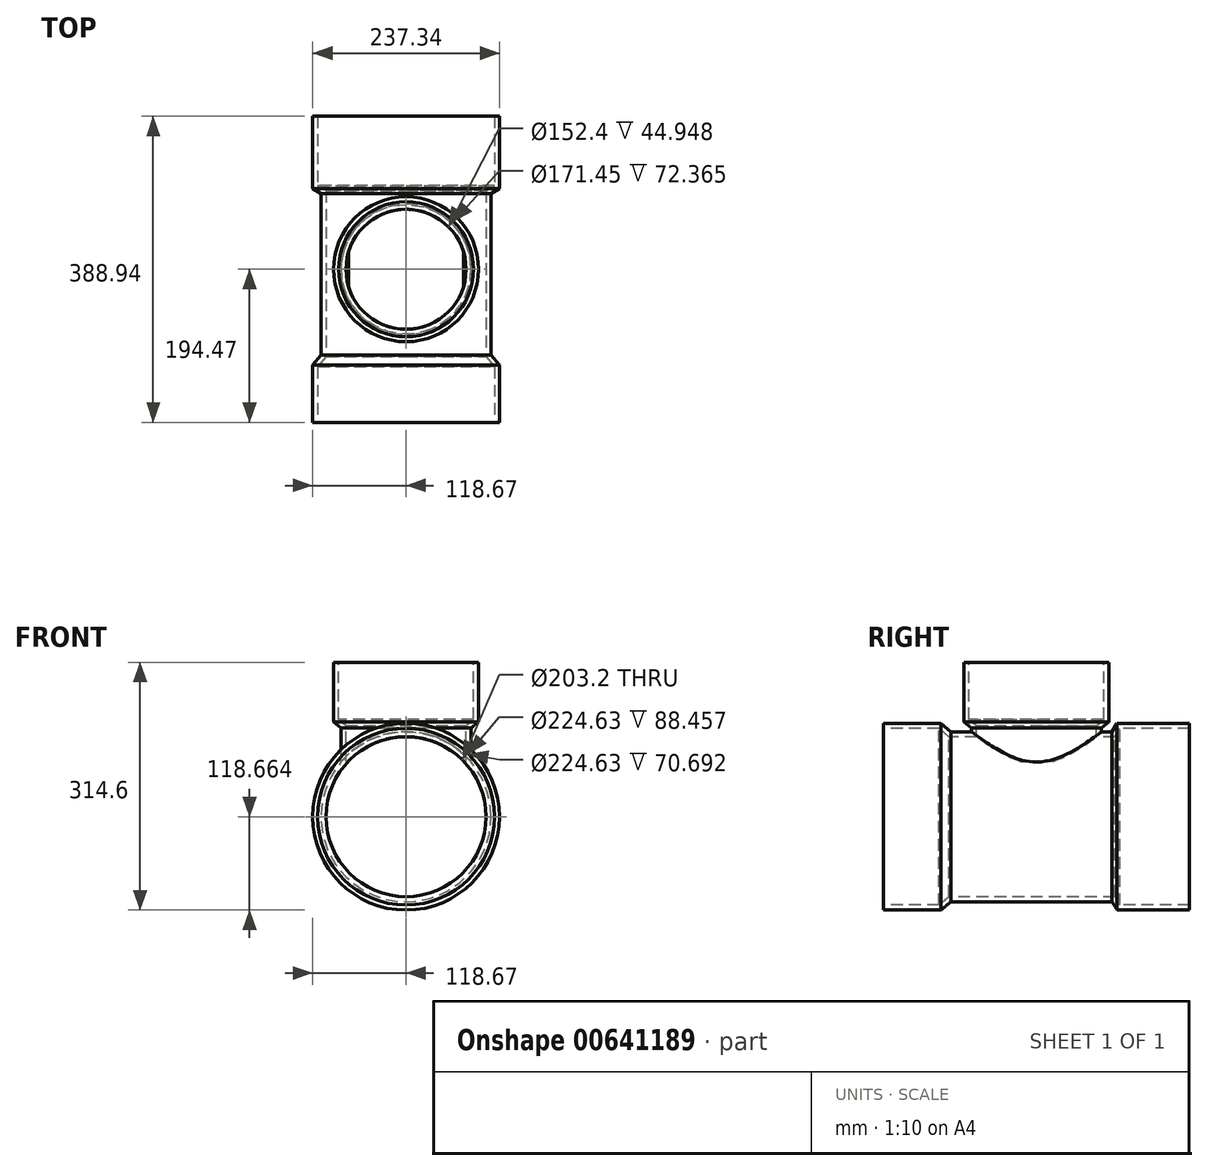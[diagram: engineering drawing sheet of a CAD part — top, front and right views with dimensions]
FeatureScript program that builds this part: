
annotation { "Feature Type Name" : "Feature", "Feature Type Description" : "" }
export const myFeature = defineFeature(function(context is Context, id is Id, definition is map)
    precondition{}
    {
        {
            var Q0;
            Q0=qCreatedBy(makeId("Right.planeOp"),FACE);
            var sketch = newSketch(context, id + "F0", { "sketchPlane" : qUnion([Q0])});
            skLineSegment(sketch, "E0", {"start": v(0, 0) * mm, "end": v(0, -195.94) * mm});
            skLineSegment(sketch, "E1", {"start": v(0, -195.94) * mm, "end": v(194.47, -195.94) * mm, "construction": true});
            skLineSegment(sketch, "E2", {"start": v(194.47, -77.27) * mm, "end": v(102.4, -77.27) * mm});
            skLineSegment(sketch, "E3", {"start": v(96.04, -94.34) * mm, "end": v(96.04, -195.94) * mm, "construction": true});
            skLineSegment(sketch, "E4", {"start": v(0, -195.94) * mm, "end": v(-194.47, -195.94) * mm, "construction": true});
            skLineSegment(sketch, "E5", {"start": v(102.4, -77.27) * mm, "end": v(96.04, -87.99) * mm});
            skLineSegment(sketch, "E6.0", {"start": v(106.01, -83.62) * mm, "end": v(103.42, -87.99) * mm});
            skLineSegment(sketch, "E6.1", {"start": v(194.47, -83.62) * mm, "end": v(106.01, -83.62) * mm});
            skLineSegment(sketch, "E7", {"start": v(96.04, -87.99) * mm, "end": v(-108.74, -87.99) * mm});
            skLineSegment(sketch, "E8.0", {"start": v(96.04, -94.34) * mm, "end": v(-108.74, -94.34) * mm});
            skLineSegment(sketch, "E9", {"start": v(103.42, -87.99) * mm, "end": v(99.66, -94.34) * mm});
            skLineSegment(sketch, "E10", {"start": v(99.66, -94.34) * mm, "end": v(96.04, -94.34) * mm});
            skLineSegment(sketch, "E11", {"start": v(194.47, -77.27) * mm, "end": v(194.47, -83.62) * mm});
            skLineSegment(sketch, "E12", {"start": v(194.47, -83.62) * mm, "end": v(194.47, -195.94) * mm, "construction": true});
            skLineSegment(sketch, "E13", {"start": v(-194.47, -77.27) * mm, "end": v(-121.46, -77.27) * mm});
            skLineSegment(sketch, "E14", {"start": v(-108.74, -94.34) * mm, "end": v(-108.74, -195.94) * mm, "construction": true});
            skLineSegment(sketch, "E15", {"start": v(-121.46, -77.27) * mm, "end": v(-108.74, -87.99) * mm});
            skLineSegment(sketch, "E16.0", {"start": v(-123.78, -83.62) * mm, "end": v(-112.84, -92.84) * mm});
            skLineSegment(sketch, "E16.1", {"start": v(-194.47, -83.62) * mm, "end": v(-123.78, -83.62) * mm});
            skLineSegment(sketch, "E17", {"start": v(-112.84, -92.84) * mm, "end": v(-111.06, -94.34) * mm});
            skLineSegment(sketch, "E18", {"start": v(-111.06, -94.34) * mm, "end": v(-108.74, -94.34) * mm});
            skLineSegment(sketch, "E19", {"start": v(-194.47, -77.27) * mm, "end": v(-194.47, -83.62) * mm});
            skSolve(sketch);
        }
        {
            var Q0;
            Q0=qCreatedBy(makeId("Top.planeOp"),FACE);
            var sketch = newSketch(context, id + "F1", { "sketchPlane" : qUnion([Q0])});
            skCircle(sketch, "E20", {"center": v(0, 0) * mm, "radius": 76.2 * mm});
            skCircle(sketch, "E21.0", {"center": v(0, 0) * mm, "radius": 69.85 * mm});
            skSolve(sketch);
        }
        {
            var Q0;
            Q0=makeQuery(id+"F0.imprint","IMPRINT",FACE,{"disambiguationData":[TD([[makeQuery(id+"F0.imprint","IMPRINT",EDGE,{"derivedFrom":sQuery(id+"F0.wireOp",EDGE,"E2")}),1.0]])]});
            var Q1;
            Q1=makeQuery(id+"F0.imprint","IMPRINT",FACE,{"disambiguationData":[TD([[makeQuery(id+"F0.imprint","IMPRINT",EDGE,{"derivedFrom":sQuery(id+"F0.wireOp",EDGE,"E13")}),-1.0]])]});
            var Q2;
            Q2=sQuery(id+"F0.wireOp",EDGE,"E1");
            revolve(context, id + "F2", {"entities" : qUnion([Q0, Q1]), "axis" : qUnion([Q2]), "revolveType" : RevolveType.FULL});
        }
        {
            var Q0;
            Q0=qCreatedBy(makeId("Right.planeOp"),FACE);
            var sketch = newSketch(context, id + "F3", { "sketchPlane" : qUnion([Q0])});
            skLineSegment(sketch, "E22", {"start": v(0, 0) * mm, "end": v(-92.08, 0) * mm, "construction": true});
            skLineSegment(sketch, "E23", {"start": v(-92.08, 0) * mm, "end": v(-85.73, 0) * mm});
            skLineSegment(sketch, "E24", {"start": v(-92.08, 0) * mm, "end": v(-92.08, -75.29) * mm});
            skLineSegment(sketch, "E25", {"start": v(0, 0) * mm, "end": v(0, -92.87) * mm, "construction": true});
            skLineSegment(sketch, "E26", {"start": v(-92.08, -75.29) * mm, "end": v(-92.08, -83.45) * mm, "construction": true});
            skLineSegment(sketch, "E27", {"start": v(0, -83.45) * mm, "end": v(-76.2, -83.45) * mm, "construction": true});
            skLineSegment(sketch, "E28", {"start": v(-76.2, -83.45) * mm, "end": v(-76.2, -92.87) * mm});
            skLineSegment(sketch, "E29.0", {"start": v(-82.55, -83.45) * mm, "end": v(-82.55, -92.87) * mm});
            skLineSegment(sketch, "E30", {"start": v(-82.55, -92.87) * mm, "end": v(-76.2, -92.87) * mm});
            skLineSegment(sketch, "E31", {"start": v(-92.08, -75.29) * mm, "end": v(-82.55, -83.45) * mm});
            skLineSegment(sketch, "E32.0", {"start": v(-85.73, -72.36) * mm, "end": v(-78.42, -78.63) * mm});
            skLineSegment(sketch, "E32.1", {"start": v(-85.73, 0) * mm, "end": v(-85.73, -72.36) * mm});
            skLineSegment(sketch, "E33", {"start": v(-78.42, -78.63) * mm, "end": v(-76.5, -80.27) * mm});
            skLineSegment(sketch, "E34", {"start": v(-76.2, -83.45) * mm, "end": v(-76.2, -80.55) * mm});
            skLineSegment(sketch, "E35", {"start": v(-76.5, -80.27) * mm, "end": v(-76.2, -80.53) * mm});
            skLineSegment(sketch, "E36", {"start": v(-76.2, -80.55) * mm, "end": v(-76.2, -80.53) * mm});
            skSolve(sketch);
        }
        {
            var Q0;
            Q0=makeQuery(id+"F3.imprint","IMPRINT",FACE,{"disambiguationData":[TD([[makeQuery(id+"F3.imprint","IMPRINT",EDGE,{"derivedFrom":sQuery(id+"F3.wireOp",EDGE,"E23")}),-1.0]])]});
            var Q1;
            Q1=sQuery(id+"F3.wireOp",EDGE,"E25");
            revolve(context, id + "F4", {"operationType" : NewBodyOperationType.ADD, "entities" : qUnion([Q0]), "axis" : qUnion([Q1]), "revolveType" : RevolveType.FULL});
        }
        {
            var Q0;
            Q0=makeQuery(id+"F1.imprint","IMPRINT",FACE,{"disambiguationData":[TD([[makeQuery(id+"F1.imprint","IMPRINT",EDGE,{"derivedFrom":sQuery(id+"F1.wireOp",EDGE,"E20")}),1.0]])]});
            var Q1;
            Q1=makeQuery(id+"F1.imprint","IMPRINT",FACE,{"disambiguationData":[TD([[makeQuery(id+"F1.imprint","IMPRINT",EDGE,{"derivedFrom":sQuery(id+"F1.wireOp",EDGE,"E21.0")}),1.0]])]});
            extrude(context, id + "F5", {"entities" : qUnion([Q0, Q1]), "operationType" : NewBodyOperationType.REMOVE, "oppositeDirection" : true, "depth" : 125.48 * mm, "offsetDistance" : 25.4 * mm});
        }
        {
            var Q0;
            Q0=makeQuery(id+"F4.boolean.opBoolean","SPLIT",FACE,{"disambiguationData":[OD(0.0)],"derivedFrom":makeQuery(id+"F4.opRevolve","SWEPT_FACE",FACE,{"disambiguationData":[OSD([sQuery(id+"F3.wireOp",EDGE,"E30")])]})});
            var Q1;
            Q1=makeQuery(id+"F4.boolean.opBoolean","SPLIT",FACE,{"disambiguationData":[OD(1.0)],"derivedFrom":makeQuery(id+"F4.opRevolve","SWEPT_FACE",FACE,{"disambiguationData":[OSD([sQuery(id+"F3.wireOp",EDGE,"E30")])]})});
            var Q2;
            Q2=makeQuery(id+"F2.opRevolve","SWEPT_BODY",BODY,{"disambiguationData":[OSD([sQuery(id+"F0.wireOp",EDGE,"E2"),sQuery(id+"F0.wireOp",EDGE,"E5"),sQuery(id+"F0.wireOp",EDGE,"E6.0"),sQuery(id+"F0.wireOp",EDGE,"E6.1"),sQuery(id+"F0.wireOp",EDGE,"E7"),sQuery(id+"F0.wireOp",EDGE,"E8.0"),sQuery(id+"F0.wireOp",EDGE,"E9"),sQuery(id+"F0.wireOp",EDGE,"E10"),sQuery(id+"F0.wireOp",EDGE,"E11"),sQuery(id+"F0.wireOp",EDGE,"E13"),sQuery(id+"F0.wireOp",EDGE,"E15"),sQuery(id+"F0.wireOp",EDGE,"E16.0"),sQuery(id+"F0.wireOp",EDGE,"E16.1"),sQuery(id+"F0.wireOp",EDGE,"E17"),sQuery(id+"F0.wireOp",EDGE,"E18"),sQuery(id+"F0.wireOp",EDGE,"E19")])]});
            extrude(context, id + "F6", {"entities" : qUnion([Q0, Q1]), "operationType" : NewBodyOperationType.ADD, "endBound" : BoundingType.UP_TO_BODY, "depth" : 25.4 * mm, "endBoundEntityBody" : qUnion([Q2]), "offsetDistance" : 25.4 * mm});
        }
    });
